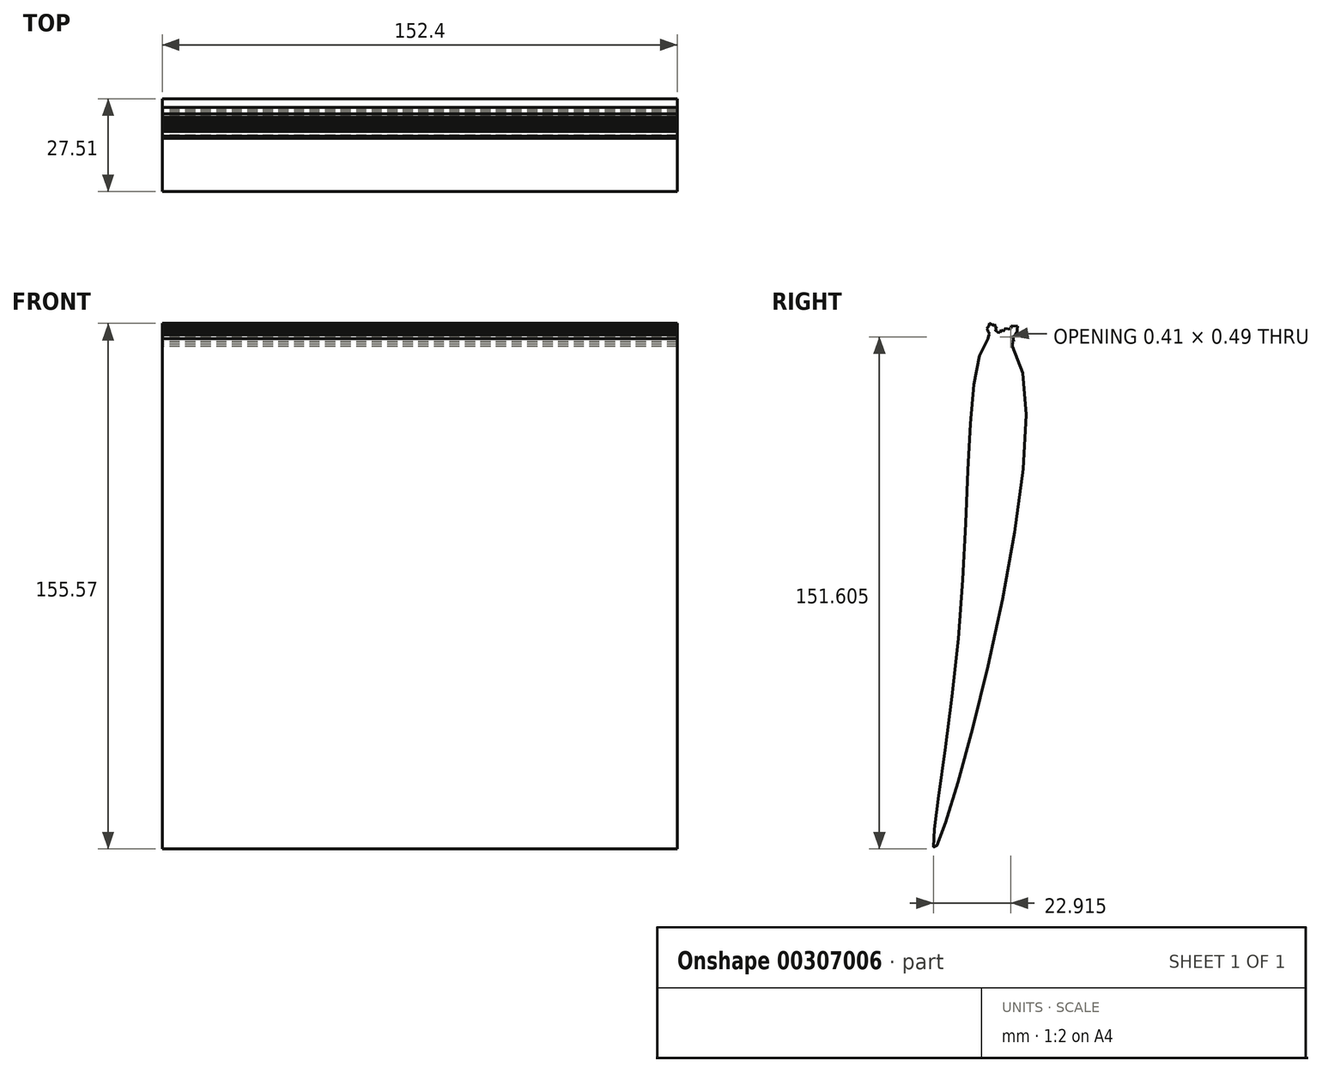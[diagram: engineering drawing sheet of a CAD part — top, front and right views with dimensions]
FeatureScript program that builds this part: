
annotation { "Feature Type Name" : "Feature", "Feature Type Description" : "" }
export const myFeature = defineFeature(function(context is Context, id is Id, definition is map)
    precondition{}
    {
        {
            var Q0;
            Q0=qCreatedBy(makeId("Right.planeOp"),FACE);
            var sketch = newSketch(context, id + "F0", { "sketchPlane" : qUnion([Q0])});
            skFitSpline(sketch, "E0", {"points": [v(13.84, 74.5) * mm, v(24.2, 60.3) * mm, v(-2.03, -76.46) * mm, v(5.04, -9.14) * mm, v(13.84, 74.5) * mm]});
            skLineSegment(sketch, "E1", {"start": v(17.96, 74.45) * mm, "end": v(20.46, 77.06) * mm});
            skLineSegment(sketch, "E2", {"start": v(20.46, 77.06) * mm, "end": v(21.45, 76.23) * mm});
            skLineSegment(sketch, "E3", {"start": v(21.45, 76.23) * mm, "end": v(19.15, 73.49) * mm});
            skLineSegment(sketch, "E4", {"start": v(19.15, 73.49) * mm, "end": v(17.96, 74.45) * mm});
            skLineSegment(sketch, "E5", {"start": v(20.46, 77.06) * mm, "end": v(21.08, 77.8) * mm});
            skPoint(sketch, "E5.endSnap0", {"position": v(20.96, 76.65) * mm});
            skLineSegment(sketch, "E6", {"start": v(21.08, 77.8) * mm, "end": v(22.01, 76.9) * mm});
            skLineSegment(sketch, "E7", {"start": v(22.01, 76.9) * mm, "end": v(21.45, 76.23) * mm});
            skLineSegment(sketch, "E8", {"start": v(15.53, 75.13) * mm, "end": v(14.77, 77.66) * mm});
            skLineSegment(sketch, "E9", {"start": v(14.77, 77.66) * mm, "end": v(13.52, 77.28) * mm});
            skLineSegment(sketch, "E10", {"start": v(13.52, 77.28) * mm, "end": v(14.28, 74.78) * mm});
            skLineSegment(sketch, "E11", {"start": v(14.28, 74.78) * mm, "end": v(15.53, 75.13) * mm});
            skLineSegment(sketch, "E12", {"start": v(19.74, 72.95) * mm, "end": v(19.9, 74.37) * mm});
            skLineSegment(sketch, "E13", {"start": v(19.9, 74.37) * mm, "end": v(20.3, 74.86) * mm});
            skLineSegment(sketch, "E14", {"start": v(20.3, 74.86) * mm, "end": v(20.27, 74.6) * mm});
            skPoint(sketch, "E14.endSnap0", {"position": v(20.1, 74.62) * mm});
            skLineSegment(sketch, "E15", {"start": v(20.27, 74.6) * mm, "end": v(19.9, 74.37) * mm});
            skLineSegment(sketch, "E16", {"start": v(19.82, 73.66) * mm, "end": v(20.47, 74.44) * mm});
            skLineSegment(sketch, "E17", {"start": v(20.47, 74.44) * mm, "end": v(20.55, 75.15) * mm});
            skLineSegment(sketch, "E18", {"start": v(20.55, 75.15) * mm, "end": v(20.98, 74.8) * mm});
            skLineSegment(sketch, "E19", {"start": v(20.98, 74.8) * mm, "end": v(20.47, 74.44) * mm});
            skLineSegment(sketch, "E20", {"start": v(21.13, 75.85) * mm, "end": v(21.98, 75.76) * mm});
            skLineSegment(sketch, "E21", {"start": v(21.98, 75.76) * mm, "end": v(21.45, 76.23) * mm});
            skLineSegment(sketch, "E22", {"start": v(22.01, 76.9) * mm, "end": v(22.02, 76.17) * mm});
            skLineSegment(sketch, "E23", {"start": v(22.02, 76.17) * mm, "end": v(21.36, 75.4) * mm});
            skLineSegment(sketch, "E24", {"start": v(21.36, 75.4) * mm, "end": v(20.55, 75.15) * mm});
            skLineSegment(sketch, "E25", {"start": v(21.36, 75.4) * mm, "end": v(21.33, 75.07) * mm});
            skLineSegment(sketch, "E26", {"start": v(21.33, 75.07) * mm, "end": v(20.98, 74.8) * mm});
            skLineSegment(sketch, "E27", {"start": v(22.02, 76.17) * mm, "end": v(21.45, 76.23) * mm});
            skLineSegment(sketch, "E28", {"start": v(20.98, 74.8) * mm, "end": v(20.88, 73.82) * mm});
            skLineSegment(sketch, "E29", {"start": v(20.88, 73.82) * mm, "end": v(19.82, 73.66) * mm});
            skLineSegment(sketch, "E30", {"start": v(22.01, 76.9) * mm, "end": v(22.1, 77.69) * mm});
            skLineSegment(sketch, "E31", {"start": v(22.1, 77.69) * mm, "end": v(21.7, 77.2) * mm});
            skLineSegment(sketch, "E32", {"start": v(21.7, 77.2) * mm, "end": v(22.1, 77.69) * mm});
            skLineSegment(sketch, "E33", {"start": v(22.1, 77.69) * mm, "end": v(21.08, 77.8) * mm});
            skLineSegment(sketch, "E34", {"start": v(21.08, 77.8) * mm, "end": v(20.26, 77.88) * mm});
            skLineSegment(sketch, "E35", {"start": v(20.26, 77.88) * mm, "end": v(20.18, 77.1) * mm});
            skLineSegment(sketch, "E36", {"start": v(20.18, 77.1) * mm, "end": v(19.2, 76.83) * mm});
            skLineSegment(sketch, "E37", {"start": v(19.2, 76.83) * mm, "end": v(18.7, 77.25) * mm});
            skLineSegment(sketch, "E38", {"start": v(18.7, 77.25) * mm, "end": v(18.59, 76.12) * mm});
            skLineSegment(sketch, "E39", {"start": v(18.59, 76.12) * mm, "end": v(18.54, 75.69) * mm});
            skLineSegment(sketch, "E40", {"start": v(18.54, 75.69) * mm, "end": v(17.8, 75.59) * mm});
            skLineSegment(sketch, "E41", {"start": v(17.8, 75.59) * mm, "end": v(17.72, 74.7) * mm});
            skLineSegment(sketch, "E42", {"start": v(17.72, 74.7) * mm, "end": v(17.96, 74.45) * mm});
            skLineSegment(sketch, "E43", {"start": v(18.7, 77.25) * mm, "end": v(17.83, 76.2) * mm});
            skLineSegment(sketch, "E44", {"start": v(17.83, 76.2) * mm, "end": v(17.26, 76.67) * mm});
            skLineSegment(sketch, "E45", {"start": v(17.26, 76.67) * mm, "end": v(16.94, 75.86) * mm});
            skLineSegment(sketch, "E46", {"start": v(16.94, 75.86) * mm, "end": v(16.22, 75.93) * mm});
            skLineSegment(sketch, "E47", {"start": v(16.22, 75.93) * mm, "end": v(15.7, 75.31) * mm});
            skLineSegment(sketch, "E48", {"start": v(16.22, 75.93) * mm, "end": v(15.63, 76.43) * mm});
            skLineSegment(sketch, "E49", {"start": v(15.63, 76.43) * mm, "end": v(15.3, 76.03) * mm});
            skLineSegment(sketch, "E50", {"start": v(15.3, 76.03) * mm, "end": v(15.38, 76.87) * mm});
            skLineSegment(sketch, "E51", {"start": v(15.38, 76.87) * mm, "end": v(14.89, 77.28) * mm});
            skLineSegment(sketch, "E52", {"start": v(14.89, 77.28) * mm, "end": v(14.77, 77.66) * mm});
            skLineSegment(sketch, "E53", {"start": v(15.38, 76.87) * mm, "end": v(15.46, 77.59) * mm});
            skLineSegment(sketch, "E54", {"start": v(15.46, 77.59) * mm, "end": v(14.89, 77.28) * mm});
            skLineSegment(sketch, "E55", {"start": v(15.46, 77.59) * mm, "end": v(15.95, 77.17) * mm});
            skLineSegment(sketch, "E56", {"start": v(15.95, 77.17) * mm, "end": v(15.38, 76.87) * mm});
            skLineSegment(sketch, "E57", {"start": v(15.46, 77.59) * mm, "end": v(15.2, 78.41) * mm});
            skLineSegment(sketch, "E58", {"start": v(15.2, 78.41) * mm, "end": v(14.77, 77.66) * mm});
            skLineSegment(sketch, "E59", {"start": v(14.77, 77.66) * mm, "end": v(14.21, 78.13) * mm});
            skPoint(sketch, "E59.endSnap0", {"position": v(14.14, 77.47) * mm});
            skLineSegment(sketch, "E60", {"start": v(14.21, 78.13) * mm, "end": v(13.52, 77.28) * mm});
            skLineSegment(sketch, "E61", {"start": v(13.52, 77.28) * mm, "end": v(13.66, 78.58) * mm});
            skLineSegment(sketch, "E62", {"start": v(13.66, 78.58) * mm, "end": v(14.99, 78.04) * mm});
            skLineSegment(sketch, "E63", {"start": v(14.99, 78.04) * mm, "end": v(15.2, 78.41) * mm});
            skLineSegment(sketch, "E64", {"start": v(13.57, 77.79) * mm, "end": v(13.01, 77.12) * mm});
            skLineSegment(sketch, "E65", {"start": v(13.01, 77.12) * mm, "end": v(13.97, 75.85) * mm});
            skLineSegment(sketch, "E66", {"start": v(13.97, 75.85) * mm, "end": v(13.3, 76.24) * mm});
            skLineSegment(sketch, "E67", {"start": v(13.3, 76.24) * mm, "end": v(13.17, 76.69) * mm});
            skLineSegment(sketch, "E68", {"start": v(13.17, 76.69) * mm, "end": v(13.01, 77.12) * mm});
            skLineSegment(sketch, "E69", {"start": v(14.28, 74.78) * mm, "end": v(13.84, 74.5) * mm});
            skLineSegment(sketch, "E70", {"start": v(13.84, 74.5) * mm, "end": v(13.64, 75.16) * mm});
            skLineSegment(sketch, "E71", {"start": v(13.64, 75.16) * mm, "end": v(14.04, 75.76) * mm});
            skLineSegment(sketch, "E72", {"start": v(14.04, 75.76) * mm, "end": v(13.3, 76.24) * mm});
            skLineSegment(sketch, "E73", {"start": v(13.3, 76.24) * mm, "end": v(13.84, 75.46) * mm});
            skLineSegment(sketch, "E74", {"start": v(20.88, 73.82) * mm, "end": v(20.98, 73.13) * mm});
            skLineSegment(sketch, "E75", {"start": v(20.98, 73.13) * mm, "end": v(20.47, 73) * mm});
            skLineSegment(sketch, "E76", {"start": v(20.47, 73) * mm, "end": v(20.64, 72.38) * mm});
            skLineSegment(sketch, "E77", {"start": v(20.64, 72.38) * mm, "end": v(20.57, 71.72) * mm});
            skLineSegment(sketch, "E78", {"start": v(20.57, 71.72) * mm, "end": v(19.74, 72.95) * mm});
            skLineSegment(sketch, "E79", {"start": v(13.64, 75.16) * mm, "end": v(13.28, 74.03) * mm});
            skLineSegment(sketch, "E80", {"start": v(13.28, 74.03) * mm, "end": v(13.84, 74.5) * mm});
            skLineSegment(sketch, "E81", {"start": v(15.38, 76.87) * mm, "end": v(15.63, 76.43) * mm});
            skLineSegment(sketch, "E82.0", {"start": v(13.64, 75.16) * mm, "end": v(20.47, 74.44) * mm, "construction": true});
            skLineSegment(sketch, "E83.0", {"start": v(13.17, 76.69) * mm, "end": v(21.98, 75.76) * mm, "construction": true});
            skLineSegment(sketch, "E84.0", {"start": v(13.3, 76.24) * mm, "end": v(16.22, 75.93) * mm, "construction": true});
            skLineSegment(sketch, "E85.0", {"start": v(13.97, 75.85) * mm, "end": v(21.33, 75.07) * mm, "construction": true});
            skLineSegment(sketch, "E86.0", {"start": v(13.01, 77.12) * mm, "end": v(22.02, 76.17) * mm, "construction": true});
            skLineSegment(sketch, "E87.0", {"start": v(13.66, 78.58) * mm, "end": v(22.1, 77.69) * mm, "construction": true});
            skLineSegment(sketch, "E88.0", {"start": v(13.57, 77.79) * mm, "end": v(22.01, 76.9) * mm, "construction": true});
            skLineSegment(sketch, "E89.0", {"start": v(14.89, 77.28) * mm, "end": v(20.96, 76.65) * mm, "construction": true});
            skLineSegment(sketch, "E90.0", {"start": v(20.1, 74.62) * mm, "end": v(20.27, 74.6) * mm, "construction": true});
            skLineSegment(sketch, "E91.0", {"start": v(17.83, 76.2) * mm, "end": v(18.59, 76.12) * mm, "construction": true});
            skLineSegment(sketch, "E92.0", {"start": v(18.54, 75.69) * mm, "end": v(21.36, 75.4) * mm, "construction": true});
            skLineSegment(sketch, "E93.0", {"start": v(13.97, 75.85) * mm, "end": v(14.21, 78.13) * mm, "construction": true});
            skLineSegment(sketch, "E94.0", {"start": v(21.36, 75.4) * mm, "end": v(21.45, 76.23) * mm, "construction": true});
            skLineSegment(sketch, "E95.0", {"start": v(13.52, 77.28) * mm, "end": v(13.57, 77.79) * mm, "construction": true});
            skLineSegment(sketch, "E96.0", {"start": v(20.96, 76.65) * mm, "end": v(21.08, 77.8) * mm, "construction": true});
            skLineSegment(sketch, "E97.0", {"start": v(19.82, 73.66) * mm, "end": v(20.26, 77.88) * mm, "construction": true});
            skLineSegment(sketch, "E98.0", {"start": v(21.98, 75.76) * mm, "end": v(22.02, 76.17) * mm, "construction": true});
            skSolve(sketch);
        }
        {
            var Q0;
            Q0=qSketchRegion(id+"F0",true);
            var Q1;
            Q1=makeQuery(id+"F0.imprint","IMPRINT",FACE,{"disambiguationData":[TD([[makeQuery(id+"F0.imprint","IMPRINT",EDGE,{"derivedFrom":sQuery(id+"F0.wireOp",EDGE,"E1")}),1.0]])]});
            var Q2;
            {var subQ3=sQuery(id+"F0.wireOp",EDGE,"E1");Q2=makeQuery(id+"F0.imprint","IMPRINT",FACE,{"disambiguationData":[TD([[makeQuery(id+"F0.imprint","IMPRINT",EDGE,{"derivedFrom":subQ3}),-1.0]])]});}
            var Q3;
            {var subQ0=sQuery(id+"F0.wireOp",EDGE,"E29");Q3=makeQuery(id+"F0.imprint","IMPRINT",FACE,{"disambiguationData":[TD([[makeQuery(id+"F0.imprint","IMPRINT",EDGE,{"derivedFrom":subQ0}),1.0]])]});}
            var Q4;
            {var subQ0=sQuery(id+"F0.wireOp",EDGE,"E78");var subQ1=sQuery(id+"F0.wireOp",EDGE,"E12");var subQ2=makeQuery(id+"F0.imprint","INTERSECT",VERTEX,{"derivedFrom":[subQ1,subQ0]});Q4=makeQuery(id+"F0.imprint","IMPRINT",FACE,{"disambiguationData":[TD([[makeQuery(id+"F0.imprint","IMPRINT",EDGE,{"disambiguationData":[TD([[subQ2,1.0]])],"derivedFrom":subQ0}),1.0]])]});}
            var Q5;
            {var subQ2=sQuery(id+"F0.wireOp",EDGE,"E8");Q5=makeQuery(id+"F0.imprint","IMPRINT",FACE,{"disambiguationData":[TD([[makeQuery(id+"F0.imprint","IMPRINT",EDGE,{"derivedFrom":subQ2}),-1.0]])]});}
            var Q6;
            {var subQ0=sQuery(id+"F0.wireOp",EDGE,"E11");Q6=makeQuery(id+"F0.imprint","IMPRINT",FACE,{"disambiguationData":[TD([[makeQuery(id+"F0.imprint","IMPRINT",EDGE,{"derivedFrom":subQ0}),1.0]])]});}
            var Q7;
            {var subQ0=sQuery(id+"F0.wireOp",EDGE,"E4");Q7=makeQuery(id+"F0.imprint","IMPRINT",FACE,{"disambiguationData":[TD([[makeQuery(id+"F0.imprint","IMPRINT",EDGE,{"derivedFrom":subQ0}),-1.0]])]});}
            var Q8;
            {var subQ0=sQuery(id+"F0.wireOp",EDGE,"E78");var subQ1=sQuery(id+"F0.wireOp",EDGE,"E0");var subQ3=makeQuery(id+"F0.imprint","INTERSECT",VERTEX,{"derivedFrom":[subQ1,subQ0]});Q8=makeQuery(id+"F0.imprint","IMPRINT",FACE,{"disambiguationData":[TD([[makeQuery(id+"F0.imprint","IMPRINT",EDGE,{"disambiguationData":[TD([[subQ3,-1.0]])],"derivedFrom":subQ1}),-1.0]])]});}
            var Q9;
            {var subQ6=sQuery(id+"F0.wireOp",EDGE,"E8");Q9=makeQuery(id+"F0.imprint","IMPRINT",FACE,{"disambiguationData":[TD([[makeQuery(id+"F0.imprint","IMPRINT",EDGE,{"derivedFrom":subQ6}),1.0]])]});}
            var Q10;
            Q10=makeQuery(id+"F0.imprint","IMPRINT",FACE,{"disambiguationData":[TD([[makeQuery(id+"F0.imprint","IMPRINT",EDGE,{"derivedFrom":sQuery(id+"F0.wireOp",EDGE,"E58")}),-1.0]])]});
            var Q11;
            {var subQ0=sQuery(id+"F0.wireOp",EDGE,"E69");Q11=makeQuery(id+"F0.imprint","IMPRINT",FACE,{"disambiguationData":[TD([[makeQuery(id+"F0.imprint","IMPRINT",EDGE,{"derivedFrom":subQ0}),-1.0]])]});}
            var Q12;
            {var subQ1=sQuery(id+"F0.wireOp",EDGE,"E70");Q12=makeQuery(id+"F0.imprint","IMPRINT",FACE,{"disambiguationData":[TD([[makeQuery(id+"F0.imprint","IMPRINT",EDGE,{"derivedFrom":subQ1}),1.0]])]});}
            var Q13;
            {var subQ0=sQuery(id+"F0.wireOp",EDGE,"E80");Q13=makeQuery(id+"F0.imprint","IMPRINT",FACE,{"disambiguationData":[TD([[makeQuery(id+"F0.imprint","IMPRINT",EDGE,{"derivedFrom":subQ0}),1.0]])]});}
            var Q14;
            {var subQ5=sQuery(id+"F0.wireOp",EDGE,"E64");Q14=makeQuery(id+"F0.imprint","IMPRINT",FACE,{"disambiguationData":[TD([[makeQuery(id+"F0.imprint","IMPRINT",EDGE,{"derivedFrom":subQ5}),1.0]])]});}
            var Q15;
            {var subQ1=sQuery(id+"F0.wireOp",EDGE,"E70");Q15=makeQuery(id+"F0.imprint","IMPRINT",FACE,{"disambiguationData":[TD([[makeQuery(id+"F0.imprint","IMPRINT",EDGE,{"derivedFrom":subQ1}),-1.0]])]});}
            var Q16;
            {var subQ0=sQuery(id+"F0.wireOp",EDGE,"E67");Q16=makeQuery(id+"F0.imprint","IMPRINT",FACE,{"disambiguationData":[TD([[makeQuery(id+"F0.imprint","IMPRINT",EDGE,{"derivedFrom":subQ0}),-1.0]])]});}
            var Q17;
            {var subQ0=sQuery(id+"F0.wireOp",EDGE,"E72");var subQ1=sQuery(id+"F0.wireOp",EDGE,"E10");var subQ2=makeQuery(id+"F0.imprint","INTERSECT",VERTEX,{"derivedFrom":[subQ1,subQ0]});Q17=makeQuery(id+"F0.imprint","IMPRINT",FACE,{"disambiguationData":[TD([[makeQuery(id+"F0.imprint","IMPRINT",EDGE,{"disambiguationData":[TD([[subQ2,-1.0]])],"derivedFrom":subQ1}),1.0]])]});}
            var Q18;
            Q18=makeQuery(id+"F0.imprint","IMPRINT",FACE,{"disambiguationData":[TD([[makeQuery(id+"F0.imprint","IMPRINT",EDGE,{"derivedFrom":sQuery(id+"F0.wireOp",EDGE,"E9")}),-1.0]])]});
            var Q19;
            Q19=makeQuery(id+"F0.imprint","IMPRINT",FACE,{"disambiguationData":[TD([[makeQuery(id+"F0.imprint","IMPRINT",EDGE,{"derivedFrom":sQuery(id+"F0.wireOp",EDGE,"E17")}),-1.0]])]});
            var Q20;
            {var subQ0=sQuery(id+"F0.wireOp",EDGE,"E65");var subQ1=sQuery(id+"F0.wireOp",EDGE,"E10");var subQ2=makeQuery(id+"F0.imprint","INTERSECT",VERTEX,{"derivedFrom":[subQ1,subQ0]});Q20=makeQuery(id+"F0.imprint","IMPRINT",FACE,{"disambiguationData":[TD([[makeQuery(id+"F0.imprint","IMPRINT",EDGE,{"disambiguationData":[TD([[subQ2,-1.0]])],"derivedFrom":subQ1}),1.0]])]});}
            var Q21;
            Q21=makeQuery(id+"F0.imprint","IMPRINT",FACE,{"disambiguationData":[TD([[makeQuery(id+"F0.imprint","IMPRINT",EDGE,{"derivedFrom":sQuery(id+"F0.wireOp",EDGE,"E18")}),1.0]])]});
            var Q22;
            Q22=makeQuery(id+"F0.imprint","IMPRINT",FACE,{"disambiguationData":[TD([[makeQuery(id+"F0.imprint","IMPRINT",EDGE,{"derivedFrom":sQuery(id+"F0.wireOp",EDGE,"E49")}),-1.0]])]});
            var Q23;
            {var subQ2=sQuery(id+"F0.wireOp",EDGE,"E32");Q23=makeQuery(id+"F0.imprint","IMPRINT",FACE,{"disambiguationData":[TD([[makeQuery(id+"F0.imprint","IMPRINT",EDGE,{"derivedFrom":subQ2}),1.0]])]});}
            var Q24;
            {var subQ0=sQuery(id+"F0.wireOp",EDGE,"E66");var subQ1=sQuery(id+"F0.wireOp",EDGE,"E10");var subQ2=makeQuery(id+"F0.imprint","INTERSECT",VERTEX,{"derivedFrom":[subQ1,subQ0]});Q24=makeQuery(id+"F0.imprint","IMPRINT",FACE,{"disambiguationData":[TD([[makeQuery(id+"F0.imprint","IMPRINT",EDGE,{"disambiguationData":[TD([[subQ2,-1.0]])],"derivedFrom":subQ1}),-1.0]])]});}
            var Q25;
            Q25=makeQuery(id+"F0.imprint","IMPRINT",FACE,{"disambiguationData":[TD([[makeQuery(id+"F0.imprint","IMPRINT",EDGE,{"derivedFrom":sQuery(id+"F0.wireOp",EDGE,"E2")}),1.0]])]});
            var Q26;
            {var subQ5=sQuery(id+"F0.wireOp",EDGE,"E73");Q26=makeQuery(id+"F0.imprint","IMPRINT",FACE,{"disambiguationData":[TD([[makeQuery(id+"F0.imprint","IMPRINT",EDGE,{"derivedFrom":subQ5}),1.0]])]});}
            var Q27;
            {var subQ1=sQuery(id+"F0.wireOp",EDGE,"E14");Q27=makeQuery(id+"F0.imprint","IMPRINT",FACE,{"disambiguationData":[TD([[makeQuery(id+"F0.imprint","IMPRINT",EDGE,{"derivedFrom":subQ1}),1.0]])]});}
            var Q28;
            Q28=makeQuery(id+"F0.imprint","IMPRINT",FACE,{"disambiguationData":[TD([[makeQuery(id+"F0.imprint","IMPRINT",EDGE,{"derivedFrom":sQuery(id+"F0.wireOp",EDGE,"E16")}),-1.0]])]});
            var Q29;
            {var subQ0=sQuery(id+"F0.wireOp",EDGE,"E24");Q29=makeQuery(id+"F0.imprint","IMPRINT",FACE,{"disambiguationData":[TD([[makeQuery(id+"F0.imprint","IMPRINT",EDGE,{"derivedFrom":subQ0}),-1.0]])]});}
            var Q30;
            Q30=makeQuery(id+"F0.imprint","IMPRINT",FACE,{"disambiguationData":[TD([[makeQuery(id+"F0.imprint","IMPRINT",EDGE,{"derivedFrom":sQuery(id+"F0.wireOp",EDGE,"E13")}),-1.0]])]});
            var Q31;
            {var subQ0=sQuery(id+"F0.wireOp",EDGE,"E21");var subQ1=sQuery(id+"F0.wireOp",EDGE,"E20");var subQ2=makeQuery(id+"F0.imprint","INTERSECT",VERTEX,{"derivedFrom":[subQ1,subQ0]});Q31=makeQuery(id+"F0.imprint","IMPRINT",FACE,{"disambiguationData":[TD([[makeQuery(id+"F0.imprint","IMPRINT",EDGE,{"disambiguationData":[TD([[subQ2,1.0]])],"derivedFrom":subQ1}),1.0]])]});}
            var Q32;
            Q32=makeQuery(id+"F0.imprint","IMPRINT",FACE,{"disambiguationData":[TD([[makeQuery(id+"F0.imprint","IMPRINT",EDGE,{"derivedFrom":sQuery(id+"F0.wireOp",EDGE,"E53")}),-1.0]])]});
            var Q33;
            {var subQ0=sQuery(id+"F0.wireOp",EDGE,"E30");Q33=makeQuery(id+"F0.imprint","IMPRINT",FACE,{"disambiguationData":[TD([[makeQuery(id+"F0.imprint","IMPRINT",EDGE,{"derivedFrom":subQ0}),1.0]])]});}
            var Q34;
            Q34=makeQuery(id+"F0.imprint","IMPRINT",FACE,{"disambiguationData":[TD([[makeQuery(id+"F0.imprint","IMPRINT",EDGE,{"derivedFrom":sQuery(id+"F0.wireOp",EDGE,"E7")}),1.0]])]});
            var Q35;
            Q35=makeQuery(id+"F0.imprint","IMPRINT",FACE,{"disambiguationData":[TD([[makeQuery(id+"F0.imprint","IMPRINT",EDGE,{"derivedFrom":sQuery(id+"F0.wireOp",EDGE,"E51")}),-1.0]])]});
            var Q36;
            Q36=makeQuery(id+"F0.imprint","IMPRINT",FACE,{"disambiguationData":[TD([[makeQuery(id+"F0.imprint","IMPRINT",EDGE,{"derivedFrom":sQuery(id+"F0.wireOp",EDGE,"E52")}),-1.0]])]});
            var Q37;
            {var subQ1=sQuery(id+"F0.wireOp",EDGE,"E3");var subQ3=sQuery(id+"F0.wireOp",EDGE,"E20");var subQ4=makeQuery(id+"F0.imprint","INTERSECT",VERTEX,{"derivedFrom":[subQ1,subQ3]});Q37=makeQuery(id+"F0.imprint","IMPRINT",FACE,{"disambiguationData":[TD([[makeQuery(id+"F0.imprint","IMPRINT",EDGE,{"disambiguationData":[TD([[subQ4,-1.0]])],"derivedFrom":subQ3}),1.0]])]});}
            var Q38;
            {var subQ0=sQuery(id+"F0.wireOp",EDGE,"E27");Q38=makeQuery(id+"F0.imprint","IMPRINT",FACE,{"disambiguationData":[TD([[makeQuery(id+"F0.imprint","IMPRINT",EDGE,{"derivedFrom":subQ0}),1.0]])]});}
            var Q39;
            {var subQ4=sQuery(id+"F0.wireOp",EDGE,"E4");Q39=makeQuery(id+"F0.imprint","IMPRINT",FACE,{"disambiguationData":[TD([[makeQuery(id+"F0.imprint","IMPRINT",EDGE,{"derivedFrom":subQ4}),1.0]])]});}
            extrude(context, id + "F1", {"entities" : qUnion([Q0, Q1, Q2, Q3, Q4, Q5, Q6, Q7, Q8, Q9, Q10, Q11, Q12, Q13, Q14, Q15, Q16, Q17, Q18, Q19, Q20, Q21, Q22, Q23, Q24, Q25, Q26, Q27, Q28, Q29, Q30, Q31, Q32, Q33, Q34, Q35, Q36, Q37, Q38, Q39]), "depth" : 76.2 * mm, "hasSecondDirection" : true, "secondDirectionOppositeDirection" : true, "secondDirectionDepth" : 76.2 * mm});
        }
    });
